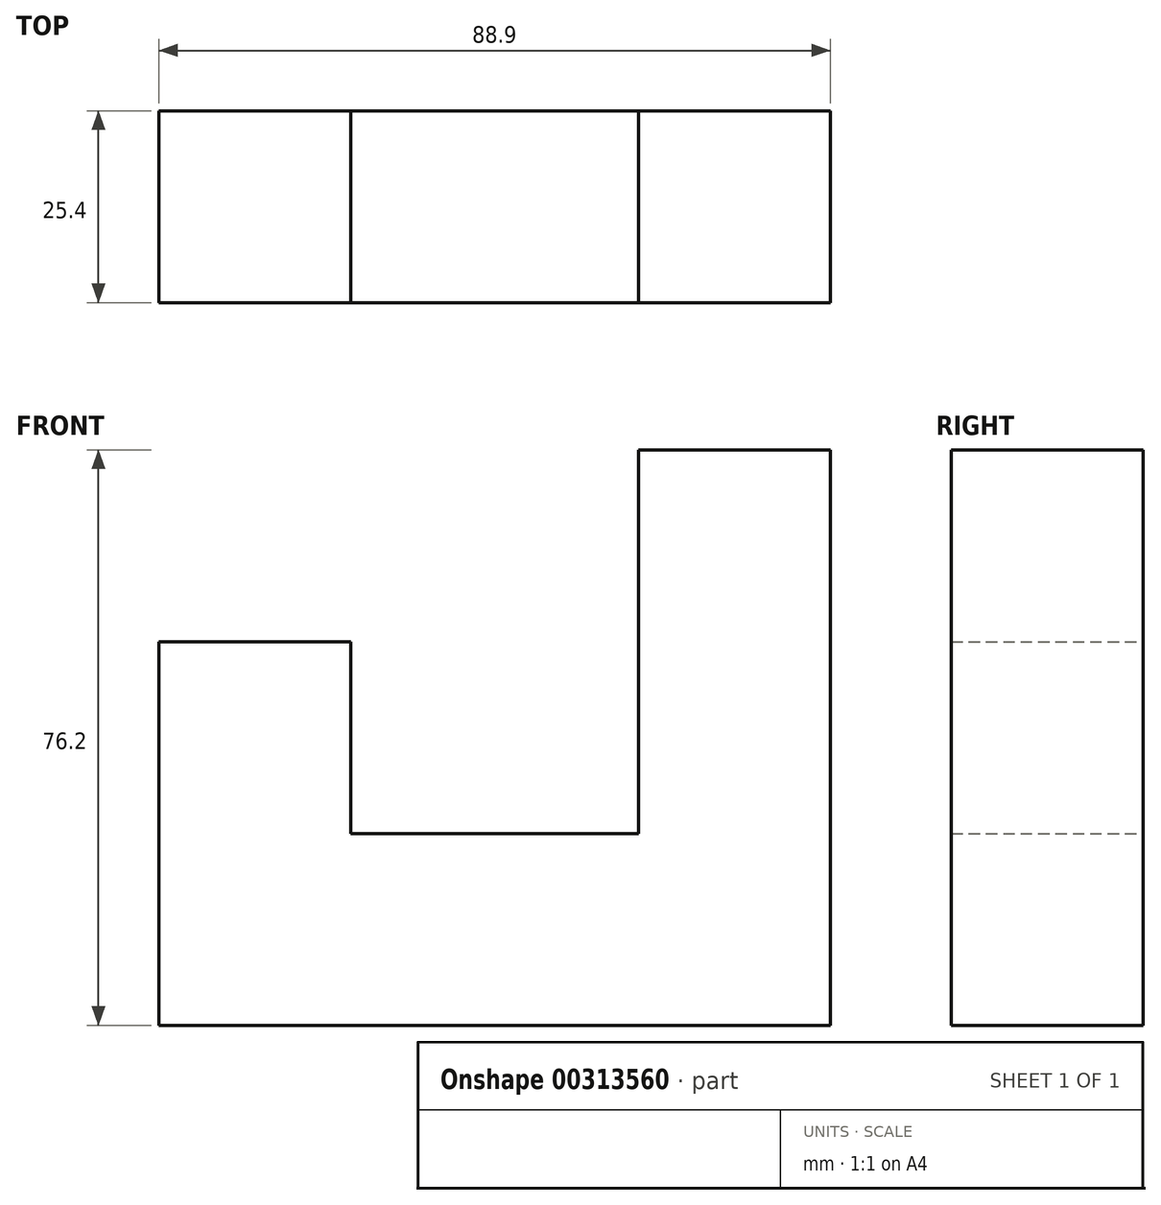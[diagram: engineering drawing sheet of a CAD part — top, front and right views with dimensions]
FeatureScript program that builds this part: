
annotation { "Feature Type Name" : "Feature", "Feature Type Description" : "" }
export const myFeature = defineFeature(function(context is Context, id is Id, definition is map)
    precondition{}
    {
        {
            var Q0;
            Q0=qCreatedBy(makeId("Front.planeOp"),FACE);
            var sketch = newSketch(context, id + "F0", { "sketchPlane" : qUnion([Q0])});
            skLineSegment(sketch, "E0", {"start": v(-40.74, -44.1) * mm, "end": v(48.16, -44.1) * mm});
            skLineSegment(sketch, "E1", {"start": v(48.16, -44.1) * mm, "end": v(48.16, 32.1) * mm});
            skLineSegment(sketch, "E2", {"start": v(48.16, 32.1) * mm, "end": v(22.76, 32.1) * mm});
            skLineSegment(sketch, "E3", {"start": v(22.76, 32.1) * mm, "end": v(22.76, -18.7) * mm});
            skLineSegment(sketch, "E4", {"start": v(22.76, -18.7) * mm, "end": v(-15.34, -18.7) * mm});
            skLineSegment(sketch, "E5", {"start": v(-15.34, -18.7) * mm, "end": v(-15.34, 6.7) * mm});
            skLineSegment(sketch, "E6", {"start": v(-15.34, 6.7) * mm, "end": v(-40.74, 6.7) * mm});
            skLineSegment(sketch, "E7", {"start": v(-40.74, 6.7) * mm, "end": v(-40.74, -44.1) * mm});
            skSolve(sketch);
        }
        {
            var Q0;
            Q0=makeQuery(id+"F0.imprint","IMPRINT",FACE,{"disambiguationData":[TD([[makeQuery(id+"F0.imprint","IMPRINT",EDGE,{"derivedFrom":sQuery(id+"F0.wireOp",EDGE,"E0")}),1.0]])]});
            extrude(context, id + "F1", {"entities" : qUnion([Q0]), "depth" : 25.4 * mm});
        }
    });
